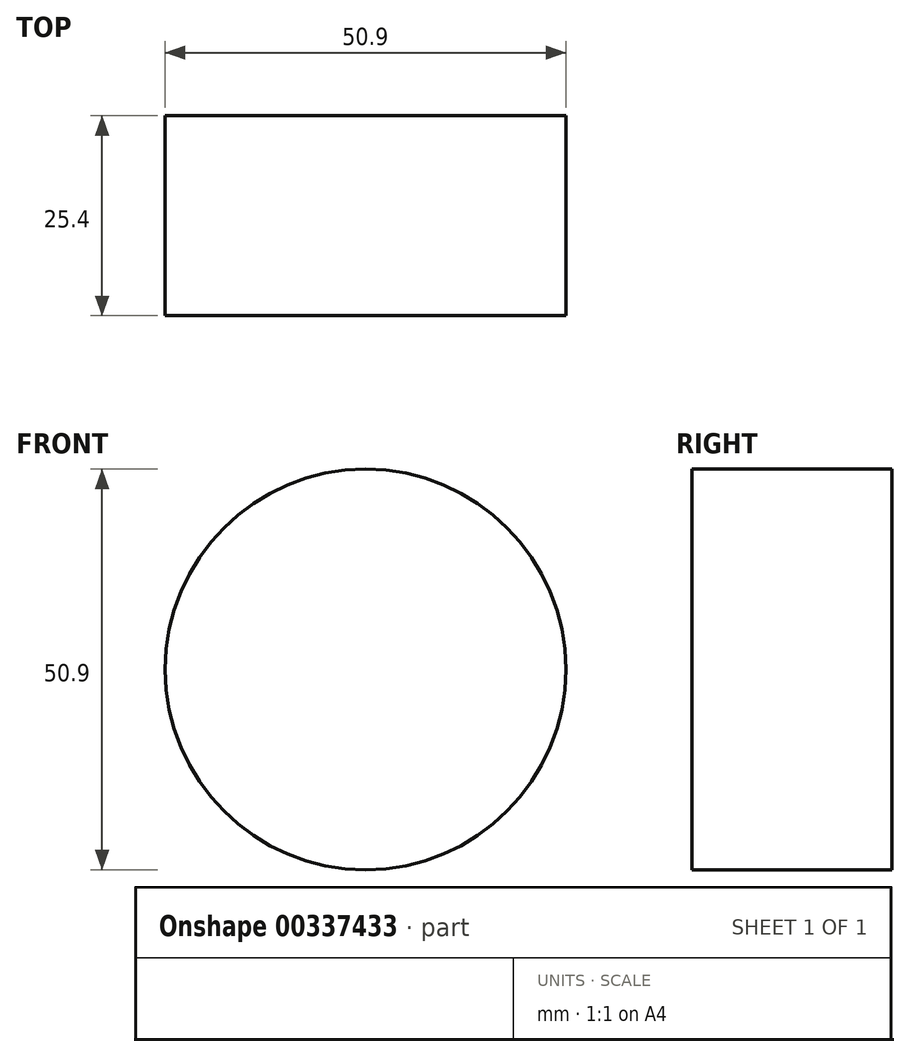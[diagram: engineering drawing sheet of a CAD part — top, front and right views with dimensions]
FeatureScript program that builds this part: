
annotation { "Feature Type Name" : "Feature", "Feature Type Description" : "" }
export const myFeature = defineFeature(function(context is Context, id is Id, definition is map)
    precondition{}
    {
        {
            var Q0;
            Q0=qCreatedBy(makeId("Front.planeOp"),FACE);
            var sketch = newSketch(context, id + "F0", { "sketchPlane" : qUnion([Q0])});
            skCircle(sketch, "E0", {"center": v(0, 0) * mm, "radius": 25.45 * mm});
            skSolve(sketch);
        }
        {
            var Q0;
            Q0=makeQuery(id+"F0.imprint","IMPRINT",FACE,{"disambiguationData":[TD([[makeQuery(id+"F0.imprint","IMPRINT",EDGE,{"derivedFrom":sQuery(id+"F0.wireOp",EDGE,"E0")}),1.0]])]});
            extrude(context, id + "F1", {"entities" : qUnion([Q0]), "depth" : 25.4 * mm});
        }
    });
